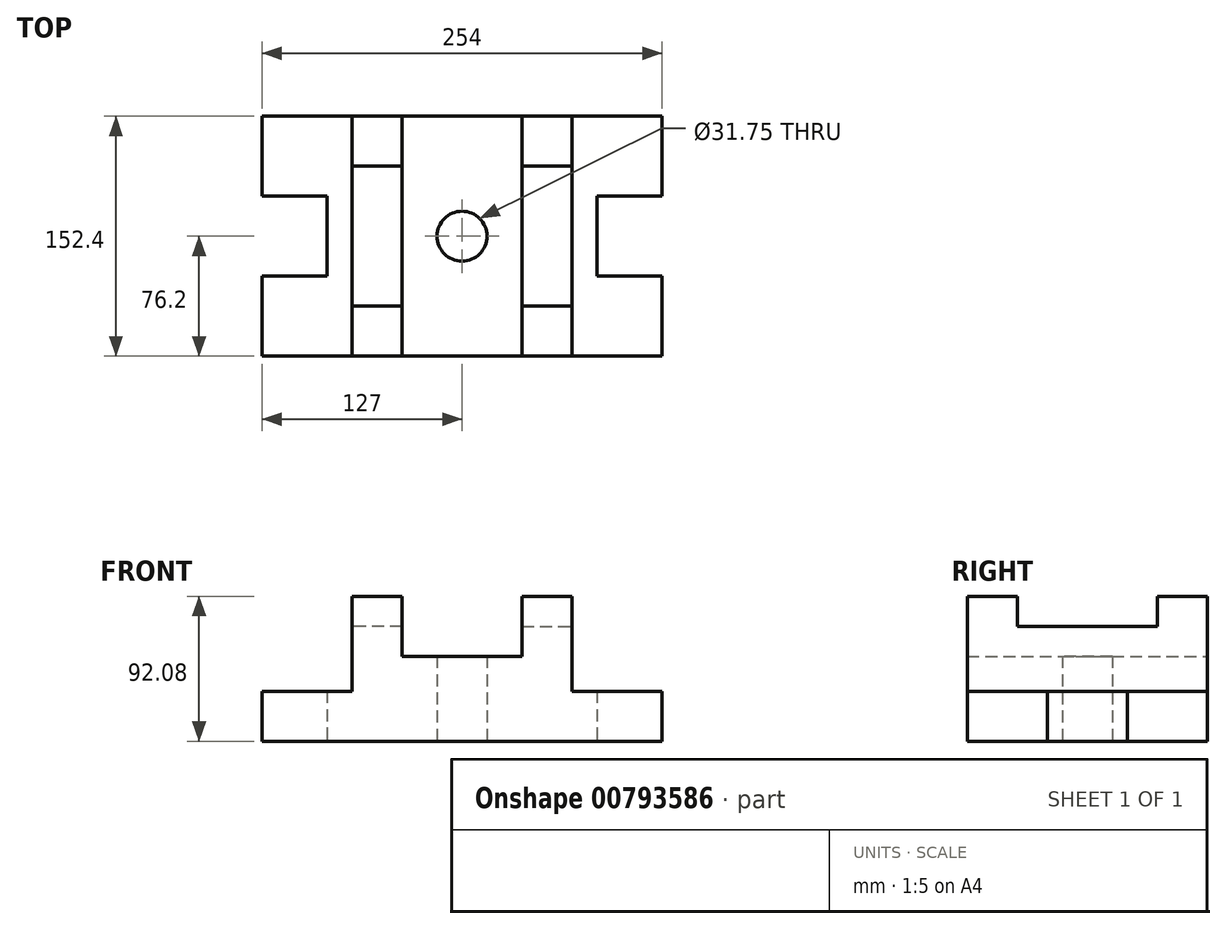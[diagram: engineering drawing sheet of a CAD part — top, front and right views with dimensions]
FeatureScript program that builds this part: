
annotation { "Feature Type Name" : "Feature", "Feature Type Description" : "" }
export const myFeature = defineFeature(function(context is Context, id is Id, definition is map)
    precondition{}
    {
        {
            var Q0;
            Q0=qCreatedBy(makeId("Top.planeOp"),FACE);
            var sketch = newSketch(context, id + "F0", { "sketchPlane" : qUnion([Q0])});
            skCircle(sketch, "E0", {"center": v(0, 0) * mm, "radius": 15.88 * mm});
            skLineSegment(sketch, "E1", {"start": v(0, -76.2) * mm, "end": v(127, -76.2) * mm});
            skLineSegment(sketch, "E2", {"start": v(127, -76.2) * mm, "end": v(127, -25.4) * mm});
            skLineSegment(sketch, "E3", {"start": v(127, -25.4) * mm, "end": v(85.72, -25.4) * mm});
            skLineSegment(sketch, "E4", {"start": v(85.72, -25.4) * mm, "end": v(85.72, 0) * mm});
            skLineSegment(sketch, "E5", {"start": v(38.1, -76.2) * mm, "end": v(38.1, 0) * mm});
            skLineSegment(sketch, "E6", {"start": v(38.1, -44.45) * mm, "end": v(69.85, -44.45) * mm});
            skLineSegment(sketch, "E7", {"start": v(69.85, -44.45) * mm, "end": v(69.85, -76.2) * mm});
            skLineSegment(sketch, "E8", {"start": v(69.85, -44.45) * mm, "end": v(69.85, 0) * mm});
            skLineSegment(sketch, "E9.MirrorCS", {"start": v(-38.1, -76.2) * mm, "end": v(-38.1, 0) * mm});
            skLineSegment(sketch, "E10.MirrorCS", {"start": v(-38.1, -44.45) * mm, "end": v(-69.85, -44.45) * mm});
            skLineSegment(sketch, "E11.MirrorCS", {"start": v(-69.85, -44.45) * mm, "end": v(-69.85, 0) * mm});
            skLineSegment(sketch, "E12.MirrorCS", {"start": v(-69.85, -44.45) * mm, "end": v(-69.85, -76.2) * mm});
            skLineSegment(sketch, "E13.MirrorCS", {"start": v(0, -76.2) * mm, "end": v(-127, -76.2) * mm});
            skLineSegment(sketch, "E14.MirrorCS", {"start": v(-127, -25.4) * mm, "end": v(-85.72, -25.4) * mm});
            skLineSegment(sketch, "E15.MirrorCS", {"start": v(-85.72, -25.4) * mm, "end": v(-85.72, 0) * mm});
            skLineSegment(sketch, "E16.MirrorCS", {"start": v(-127, -76.2) * mm, "end": v(-127, -25.4) * mm});
            skLineSegment(sketch, "E17.MirrorCS", {"start": v(38.1, 76.2) * mm, "end": v(38.1, 0) * mm});
            skLineSegment(sketch, "E18.MirrorCS", {"start": v(38.1, 44.45) * mm, "end": v(69.85, 44.45) * mm});
            skLineSegment(sketch, "E19.MirrorCS", {"start": v(69.85, 44.45) * mm, "end": v(69.85, 0) * mm});
            skLineSegment(sketch, "E20.MirrorCS", {"start": v(85.72, 25.4) * mm, "end": v(85.72, 0) * mm});
            skLineSegment(sketch, "E21.MirrorCS", {"start": v(127, 25.4) * mm, "end": v(85.72, 25.4) * mm});
            skLineSegment(sketch, "E22.MirrorCS", {"start": v(127, 76.2) * mm, "end": v(127, 25.4) * mm});
            skLineSegment(sketch, "E23.MirrorCS", {"start": v(0, 76.2) * mm, "end": v(127, 76.2) * mm});
            skLineSegment(sketch, "E24.MirrorCS", {"start": v(-85.72, 25.4) * mm, "end": v(-85.72, 0) * mm});
            skLineSegment(sketch, "E25.MirrorCS", {"start": v(-127, 25.4) * mm, "end": v(-85.72, 25.4) * mm});
            skLineSegment(sketch, "E26.MirrorCS", {"start": v(-127, 76.2) * mm, "end": v(-127, 25.4) * mm});
            skLineSegment(sketch, "E27.MirrorCS", {"start": v(-69.85, 44.45) * mm, "end": v(-69.85, 0) * mm});
            skLineSegment(sketch, "E28.MirrorCS", {"start": v(-38.1, 76.2) * mm, "end": v(-38.1, 0) * mm});
            skLineSegment(sketch, "E29.MirrorCS", {"start": v(0, 76.2) * mm, "end": v(-127, 76.2) * mm});
            skLineSegment(sketch, "E30.MirrorCS", {"start": v(-38.1, 44.45) * mm, "end": v(-69.85, 44.45) * mm});
            skLineSegment(sketch, "E31.MirrorCS", {"start": v(-69.85, 44.45) * mm, "end": v(-69.85, 76.2) * mm});
            skLineSegment(sketch, "E32.MirrorCS", {"start": v(69.85, 44.45) * mm, "end": v(69.85, 76.2) * mm});
            skSolve(sketch);
        }
        {
            var Q0;
            {var subQ10=sQuery(id+"F0.wireOp",EDGE,"E2");Q0=makeQuery(id+"F0.imprint","IMPRINT",FACE,{"disambiguationData":[TD([[makeQuery(id+"F0.imprint","IMPRINT",EDGE,{"derivedFrom":subQ10}),1.0]])]});}
            extrude(context, id + "F1", {"entities" : qUnion([Q0]), "depth" : 31.75 * mm});
        }
        {
            var Q0;
            {var subQ4=sQuery(id+"F0.wireOp",EDGE,"E6");Q0=makeQuery(id+"F0.imprint","IMPRINT",FACE,{"disambiguationData":[TD([[makeQuery(id+"F0.imprint","IMPRINT",EDGE,{"derivedFrom":subQ4}),-1.0]])]});}
            extrude(context, id + "F2", {"entities" : qUnion([Q0]), "operationType" : NewBodyOperationType.ADD, "depth" : 92.07 * mm});
        }
        {
            var Q0;
            {var subQ4=sQuery(id+"F0.wireOp",EDGE,"E6");Q0=makeQuery(id+"F0.imprint","IMPRINT",FACE,{"disambiguationData":[TD([[makeQuery(id+"F0.imprint","IMPRINT",EDGE,{"derivedFrom":subQ4}),1.0]])]});}
            extrude(context, id + "F3", {"entities" : qUnion([Q0]), "operationType" : NewBodyOperationType.ADD, "depth" : 73.02 * mm});
        }
        {
            var Q0;
            {var subQ3=sQuery(id+"F0.wireOp",EDGE,"E18.MirrorCS");Q0=makeQuery(id+"F0.imprint","IMPRINT",FACE,{"disambiguationData":[TD([[makeQuery(id+"F0.imprint","IMPRINT",EDGE,{"derivedFrom":subQ3}),1.0]])]});}
            extrude(context, id + "F4", {"entities" : qUnion([Q0]), "operationType" : NewBodyOperationType.ADD, "depth" : 92.07 * mm});
        }
        {
            var Q0;
            Q0=makeQuery(id+"F1.opExtrude","SWEPT_BODY",BODY,{"disambiguationData":[OSD([sQuery(id+"F0.wireOp",EDGE,"E1"),sQuery(id+"F0.wireOp",EDGE,"E2"),sQuery(id+"F0.wireOp",EDGE,"E3"),sQuery(id+"F0.wireOp",EDGE,"E4"),sQuery(id+"F0.wireOp",EDGE,"E7"),sQuery(id+"F0.wireOp",EDGE,"E8"),sQuery(id+"F0.wireOp",EDGE,"E19.MirrorCS"),sQuery(id+"F0.wireOp",EDGE,"E20.MirrorCS"),sQuery(id+"F0.wireOp",EDGE,"E21.MirrorCS"),sQuery(id+"F0.wireOp",EDGE,"E22.MirrorCS"),sQuery(id+"F0.wireOp",EDGE,"E23.MirrorCS"),sQuery(id+"F0.wireOp",EDGE,"E32.MirrorCS")])]});
            var Q1;
            Q1=qCreatedBy(makeId("Right.planeOp"),FACE);
            mirror(context, id + "F5", {"entities" : qUnion([Q0]), "mirrorPlane" : qUnion([Q1])});
        }
        {
            var Q0;
            Q0=makeQuery(id+"F0.imprint","IMPRINT",FACE,{"disambiguationData":[TD([[makeQuery(id+"F0.imprint","IMPRINT",EDGE,{"derivedFrom":sQuery(id+"F0.wireOp",EDGE,"E0")}),-1.0]])]});
            extrude(context, id + "F6", {"entities" : qUnion([Q0]), "operationType" : NewBodyOperationType.ADD, "depth" : 53.97 * mm});
        }
    });
